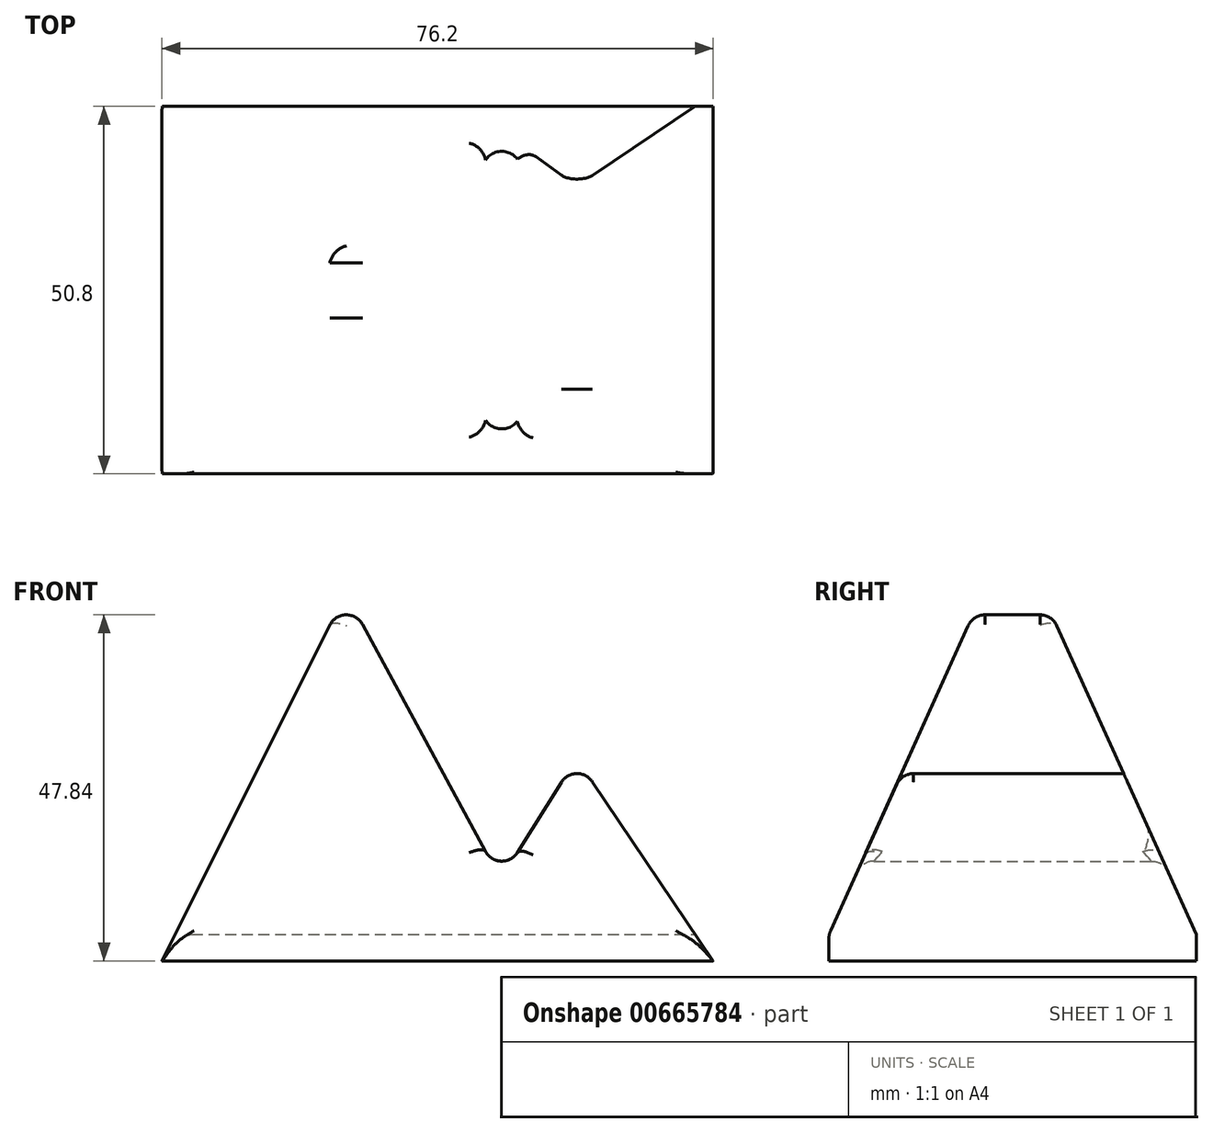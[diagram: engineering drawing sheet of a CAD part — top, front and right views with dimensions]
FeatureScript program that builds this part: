
annotation { "Feature Type Name" : "Feature", "Feature Type Description" : "" }
export const myFeature = defineFeature(function(context is Context, id is Id, definition is map)
    precondition{}
    {
        {
            var Q0;
            Q0=qCreatedBy(makeId("Top.planeOp"),FACE);
            var sketch = newSketch(context, id + "F0", { "sketchPlane" : qUnion([Q0])});
            skLineSegment(sketch, "E0.bottom", {"start": v(-50.8, 25.4) * mm, "end": v(25.4, 25.4) * mm});
            skLineSegment(sketch, "E0.top", {"start": v(-50.8, -25.4) * mm, "end": v(25.4, -25.4) * mm});
            skLineSegment(sketch, "E0.left", {"start": v(-50.8, 25.4) * mm, "end": v(-50.8, -25.4) * mm});
            skLineSegment(sketch, "E0.right", {"start": v(25.4, 25.4) * mm, "end": v(25.4, -25.4) * mm});
            skSolve(sketch);
        }
        {
            var Q0;
            Q0=makeQuery(id+"F0.imprint","IMPRINT",FACE,{"disambiguationData":[TD([[makeQuery(id+"F0.imprint","IMPRINT",EDGE,{"derivedFrom":sQuery(id+"F0.wireOp",EDGE,"E0.bottom")}),-1.0]])]});
            extrude(context, id + "F1", {"entities" : qUnion([Q0]), "depth" : 50.8 * mm, "offsetDistance" : 25.4 * mm});
        }
        {
            var Q0;
            Q0=makeQuery(id+"F1.opExtrude","SWEPT_FACE",FACE,{"disambiguationData":[OSD([sQuery(id+"F0.wireOp",EDGE,"E0.top")])]});
            var sketch = newSketch(context, id + "F2", { "sketchPlane" : qUnion([Q0])});
            skLineSegment(sketch, "E1", {"start": v(-50.8, 0) * mm, "end": v(-25.4, 50.8) * mm});
            skLineSegment(sketch, "E2", {"start": v(-25.4, 50.8) * mm, "end": v(-4, 11.28) * mm});
            skLineSegment(sketch, "E3", {"start": v(-4, 11.28) * mm, "end": v(6.5, 28) * mm});
            skLineSegment(sketch, "E4", {"start": v(6.5, 28) * mm, "end": v(25.4, 0) * mm});
            skLineSegment(sketch, "E5", {"start": v(25.4, 0) * mm, "end": v(36.36, 0) * mm});
            skLineSegment(sketch, "E6", {"start": v(36.36, 0) * mm, "end": v(36.36, 59.05) * mm});
            skLineSegment(sketch, "E7", {"start": v(36.36, 59.05) * mm, "end": v(-59.65, 59.05) * mm});
            skLineSegment(sketch, "E8", {"start": v(-59.65, 59.05) * mm, "end": v(-59.65, 0) * mm});
            skLineSegment(sketch, "E9", {"start": v(-59.65, 0) * mm, "end": v(-50.8, 0) * mm});
            skSolve(sketch);
        }
        {
            var Q0;
            Q0 = qSketchRegion(id + "F2", true);
            var Q1;
            Q1=makeQuery(id+"F1.opExtrude","SWEPT_FACE",FACE,{"disambiguationData":[OSD([sQuery(id+"F0.wireOp",EDGE,"E0.bottom")])]});
            extrude(context, id + "F3", {"entities" : qUnion([Q0]), "operationType" : NewBodyOperationType.REMOVE, "endBound" : BoundingType.UP_TO_SURFACE, "oppositeDirection" : true, "depth" : 53.34 * mm, "endBoundEntityFace" : qUnion([Q1]), "offsetDistance" : 25.4 * mm});
        }
        {
            var Q0;
            Q0=qCreatedBy(makeId("Right.planeOp"),FACE);
            var sketch = newSketch(context, id + "F4", { "sketchPlane" : qUnion([Q0])});
            skLineSegment(sketch, "E10", {"start": v(-1.65, 56.32) * mm, "end": v(-27.05, 0) * mm});
            skLineSegment(sketch, "E11", {"start": v(-27.05, 0) * mm, "end": v(-27.05, 56.32) * mm});
            skLineSegment(sketch, "E12", {"start": v(-27.05, 56.32) * mm, "end": v(-1.65, 56.32) * mm});
            skLineSegment(sketch, "E13", {"start": v(1.65, 56.15) * mm, "end": v(27.05, 56.15) * mm});
            skLineSegment(sketch, "E14", {"start": v(27.05, 56.15) * mm, "end": v(27.05, 0) * mm});
            skLineSegment(sketch, "E15", {"start": v(27.05, 0) * mm, "end": v(1.65, 56.15) * mm});
            skSolve(sketch);
        }
        {
            var Q0;
            Q0 = qSketchRegion(id + "F4", true);
            extrude(context, id + "F5", {"entities" : qUnion([Q0]), "operationType" : NewBodyOperationType.REMOVE, "endBound" : BoundingType.THROUGH_ALL, "oppositeDirection" : true, "depth" : 25.4 * mm, "offsetDistance" : 25.4 * mm, "hasSecondDirection" : true, "secondDirectionBound" : SecondDirectionBoundingType.THROUGH_ALL, "secondDirectionOppositeDirection" : false, "secondDirectionDepth" : 25.4 * mm});
        }
        {
            var Q0;
            Q0=makeQuery(id+"F3.boolean.opBoolean","COPY",EDGE,{"derivedFrom":makeQuery(id+"F3.opExtrude","SWEPT_EDGE",EDGE,{"disambiguationData":[OSD([sQuery(id+"F2.wireOp",EDGE,"E3"),sQuery(id+"F2.wireOp",EDGE,"E4")])]})});
            var Q1;
            Q1=makeQuery(id+"F3.boolean.opBoolean","COPY",EDGE,{"derivedFrom":makeQuery(id+"F3.opExtrude","SWEPT_EDGE",EDGE,{"disambiguationData":[OSD([sQuery(id+"F0.wireOp",EDGE,"E0.top"),sQuery(id+"F2.wireOp",EDGE,"E1"),sQuery(id+"F2.wireOp",EDGE,"E2")])]})});
            fillet(context, id + "F6", {"entities" : qUnion([Q0, Q1]), "radius" : 2.54 * mm, "tangentPropagation" : true, "allowEdgeOverflow" : false});
        }
        {
            var Q0;
            Q0=makeQuery(id+"F5.boolean.opBoolean","COPY",FACE,{"derivedFrom":makeQuery(id+"F5.opExtrude","SWEPT_FACE",FACE,{"disambiguationData":[OSD([sQuery(id+"F4.wireOp",EDGE,"E10")])]})});
            var Q1;
            Q1=makeQuery(id+"F3.boolean.opBoolean","COPY",EDGE,{"derivedFrom":makeQuery(id+"F3.opExtrude","SWEPT_EDGE",EDGE,{"disambiguationData":[OSD([sQuery(id+"F2.wireOp",EDGE,"E2"),sQuery(id+"F2.wireOp",EDGE,"E3")])]})});
            var Q2;
            Q2=makeQuery(id+"F5.boolean.opBoolean","INTERSECT",EDGE,{"derivedFrom":[makeQuery(id+"F3.boolean.opBoolean","COPY",FACE,{"derivedFrom":makeQuery(id+"F3.opExtrude","SWEPT_FACE",FACE,{"disambiguationData":[OSD([sQuery(id+"F2.wireOp",EDGE,"E2")])]})}),makeQuery(id+"F5.opExtrude","SWEPT_FACE",FACE,{"disambiguationData":[OSD([sQuery(id+"F4.wireOp",EDGE,"E15")])]})]});
            fillet(context, id + "F7", {"entities" : qUnion([Q0, Q1, Q2]), "radius" : 2.54 * mm, "tangentPropagation" : true, "allowEdgeOverflow" : false});
        }
    });
